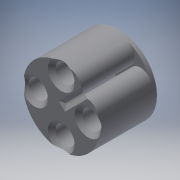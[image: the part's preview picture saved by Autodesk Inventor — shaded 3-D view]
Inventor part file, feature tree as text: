
AUTODESK INVENTOR PART (.ipt)
format: ipt  version: 2019 (Build 230136000, 136)  size: 184,320 bytes
history: native  units: mm
features: extrude x2, chamfer x2, sketch x2, fillet x1
ambient origin geometry x8: Origin, YZ Plane, XZ Plane, XY Plane, X Axis, Y Axis, Z Axis, Center Point
bodies: Solid1 (feature_tree)
feature tree (7):
  extrude  "Extrusion1"  Depth=14.0mm
  extrude  "Extrusion2"  Depth=3.0mm TaperAngle=360.0deg
  chamfer  "Chamfer1"  Distance=15.0mm
  chamfer  "Chamfer2"  Distance=14.0mm
  fillet  "Fillet1"  Radius=7.0mm
  sketch  "Sketch1"  dims[d0=20.0mm d1=14.0mm]
  sketch  "Sketch2"  dims[d2=3.0mm d3=40.0mm d5=360.0deg d7=15.0mm d8=0.0mm d9=14.0mm d10=7.0mm d11=7.0mm d12=0.5mm d13=10.0mm d14=5.0mm d15=20.0mm d16=40.0mm d18=360.0deg d20=14.0mm d21=0.0mm d22=1.0mm d23=2.0mm d24=45.0deg d25=1.0mm d26=2.0mm d27=45.0deg d28=3.0mm]
